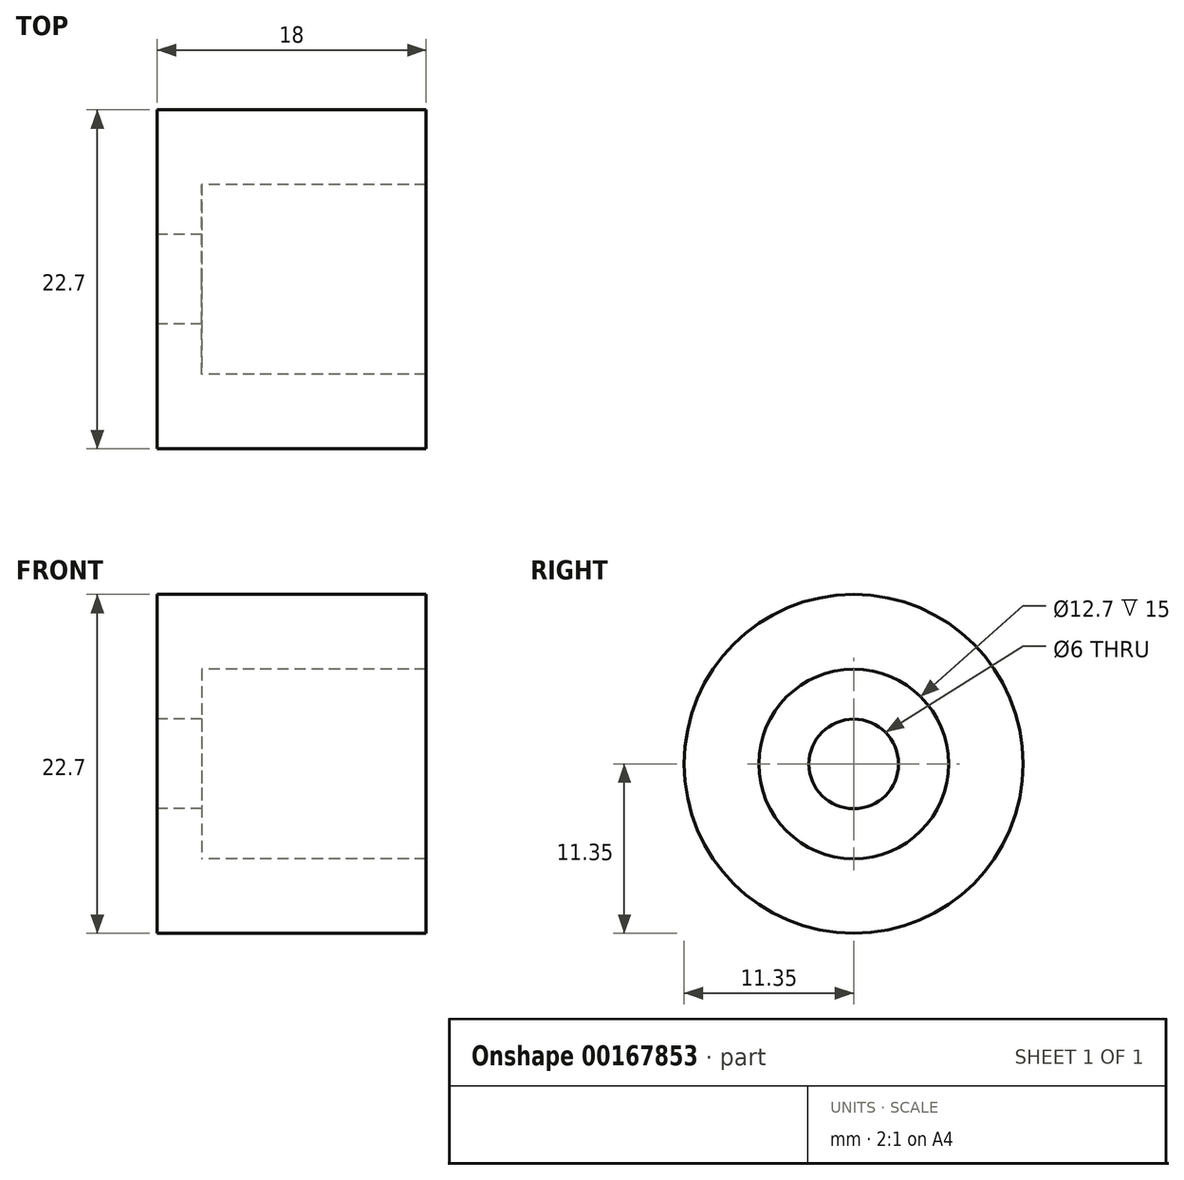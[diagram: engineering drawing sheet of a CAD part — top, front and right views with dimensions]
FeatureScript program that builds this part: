
annotation { "Feature Type Name" : "Feature", "Feature Type Description" : "" }
export const myFeature = defineFeature(function(context is Context, id is Id, definition is map)
    precondition{}
    {
        {
            var Q0;
            Q0=qCreatedBy(makeId("Front.planeOp"),FACE);
            var sketch = newSketch(context, id + "F0", { "sketchPlane" : qUnion([Q0])});
            skLineSegment(sketch, "E0", {"start": v(14.87, 6.35) * mm, "end": v(-0.13, 6.35) * mm});
            skLineSegment(sketch, "E1", {"start": v(-0.13, 6.35) * mm, "end": v(-0.13, 3) * mm});
            skLineSegment(sketch, "E2", {"start": v(-0.13, 3) * mm, "end": v(-3.13, 3) * mm});
            skLineSegment(sketch, "E3", {"start": v(-3.13, 3) * mm, "end": v(-3.13, 11.35) * mm});
            skLineSegment(sketch, "E4", {"start": v(-3.13, 11.35) * mm, "end": v(14.87, 11.35) * mm});
            skLineSegment(sketch, "E5", {"start": v(14.87, 11.35) * mm, "end": v(14.87, 6.35) * mm});
            skLineSegment(sketch, "E6", {"start": v(-6.69, 0) * mm, "end": v(10.76, 0) * mm, "construction": true});
            skSolve(sketch);
        }
        {
            var Q0;
            Q0 = qSketchRegion(id + "F0", true);
            var Q1;
            Q1=sQuery(id+"F0.wireOp",EDGE,"E6");
            revolve(context, id + "F1", {"entities" : qUnion([Q0]), "axis" : qUnion([Q1]), "revolveType" : RevolveType.FULL});
        }
    });
